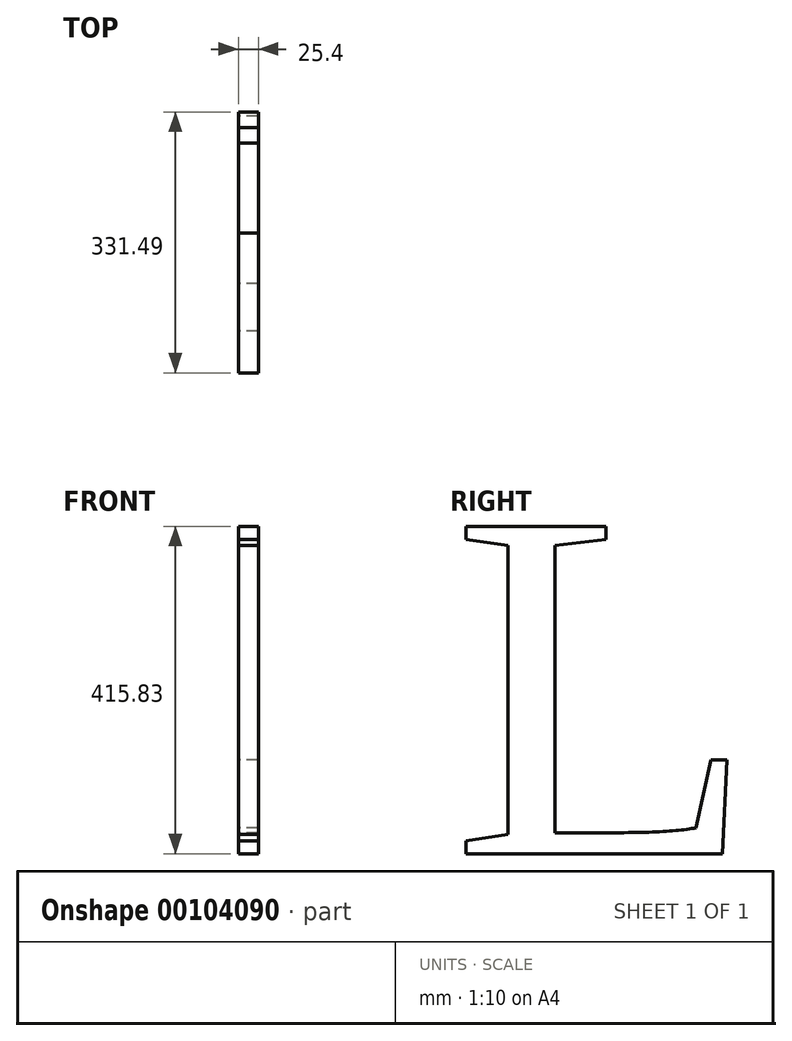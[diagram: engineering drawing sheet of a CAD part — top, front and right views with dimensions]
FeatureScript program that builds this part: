
annotation { "Feature Type Name" : "Feature", "Feature Type Description" : "" }
export const myFeature = defineFeature(function(context is Context, id is Id, definition is map)
    precondition{}
    {
        {
            var Q0;
            Q0=qCreatedBy(makeId("Right.planeOp"),FACE);
            var sketch = newSketch(context, id + "F0", { "sketchPlane" : qUnion([Q0])});
            skText(sketch, "E0", { "text": "L", "fontName": "Tinos-Regular.ttf"});
            const initialGuessF0  = {"E0": [-0.34975, 0, 1, 0, 0.4572]};
            skSetInitialGuess(sketch, initialGuessF0);
            skSolve(sketch);
        }
        {
            var Q0;
            Q0 = qSketchRegion(id + "F0", true);
            extrude(context, id + "F1", {"entities" : qUnion([Q0]), "depth" : 25.4 * mm});
        }
    });
